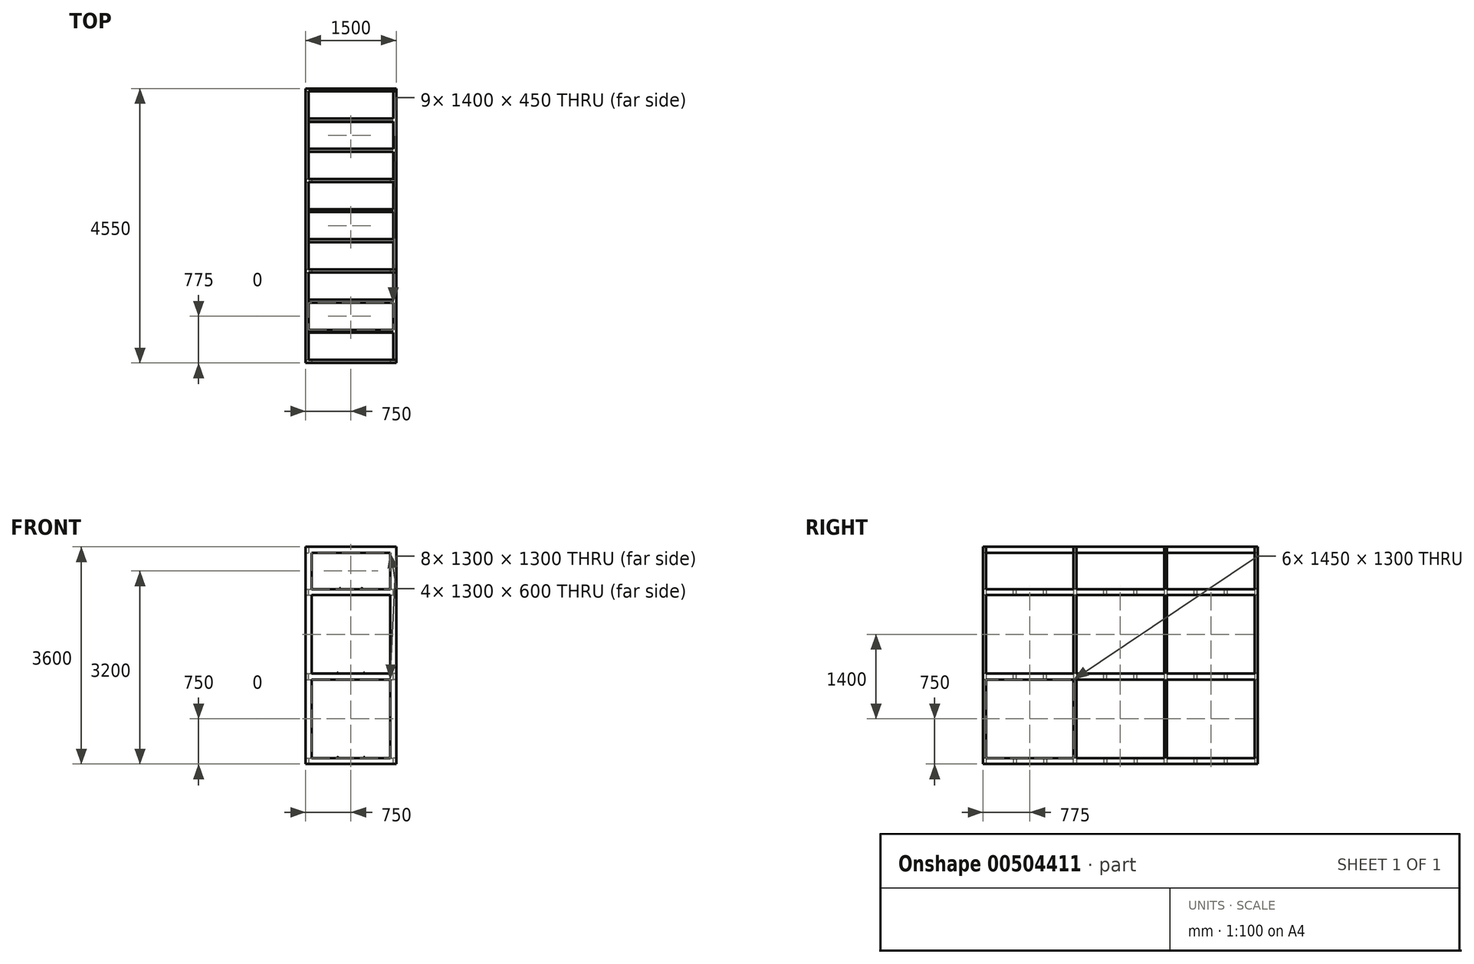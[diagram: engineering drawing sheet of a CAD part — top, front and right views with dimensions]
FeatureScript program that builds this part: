
annotation { "Feature Type Name" : "Feature", "Feature Type Description" : "" }
export const myFeature = defineFeature(function(context is Context, id is Id, definition is map)
    precondition{}
    {
        {
            var Q0;
            Q0=qCreatedBy(makeId("Front.planeOp"),FACE);
            var sketch = newSketch(context, id + "F0", { "sketchPlane" : qUnion([Q0])});
            skCircle(sketch, "E0", {"center": v(0, 700) * mm, "radius": 600 * mm});
            skCircle(sketch, "E1", {"center": v(0, 2100) * mm, "radius": 600 * mm});
            skCircle(sketch, "E2", {"center": v(0, 3275) * mm, "radius": 375 * mm});
            skSolve(sketch);
        }
        {
            var Q0;
            Q0=qCreatedBy(makeId("Front.planeOp"),FACE);
            var sketch = newSketch(context, id + "F1", { "sketchPlane" : qUnion([Q0])});
            skLineSegment(sketch, "E3.bottom", {"start": v(-750, 3600) * mm, "end": v(750, 3600) * mm});
            skLineSegment(sketch, "E3.top", {"start": v(-750, 0) * mm, "end": v(750, 0) * mm});
            skLineSegment(sketch, "E3.left", {"start": v(-750, 3600) * mm, "end": v(-750, 0) * mm});
            skLineSegment(sketch, "E3.right", {"start": v(750, 3600) * mm, "end": v(750, 0) * mm});
            skSolve(sketch);
        }
        {
            var Q0;
            Q0=makeQuery(id+"F1.imprint","IMPRINT",FACE,{"disambiguationData":[TD([[makeQuery(id+"F1.imprint","IMPRINT",EDGE,{"derivedFrom":sQuery(id+"F1.wireOp",EDGE,"E3.bottom")}),-1.0]])]});
            extrude(context, id + "F2", {"entities" : qUnion([Q0]), "depth" : 4550 * mm, "offsetDistance" : 25 * mm});
        }
        {
            var Q0;
            Q0=makeQuery(id+"F2.opExtrude","CAP_FACE",FACE,{"disambiguationData":[OSD([sQuery(id+"F1.wireOp",EDGE,"E3.bottom"),sQuery(id+"F1.wireOp",EDGE,"E3.top"),sQuery(id+"F1.wireOp",EDGE,"E3.left"),sQuery(id+"F1.wireOp",EDGE,"E3.right")])],"isStart":false});
            var sketch = newSketch(context, id + "F3", { "sketchPlane" : qUnion([Q0])});
            skLineSegment(sketch, "E4.bottom", {"start": v(-650, 1400) * mm, "end": v(650, 1400) * mm});
            skLineSegment(sketch, "E4.top", {"start": v(-650, 100) * mm, "end": v(650, 100) * mm});
            skLineSegment(sketch, "E4.left", {"start": v(-650, 1400) * mm, "end": v(-650, 100) * mm});
            skLineSegment(sketch, "E4.right", {"start": v(650, 1400) * mm, "end": v(650, 100) * mm});
            skLineSegment(sketch, "E5.bottom", {"start": v(-650, 2800) * mm, "end": v(650, 2800) * mm});
            skLineSegment(sketch, "E5.top", {"start": v(-650, 1500) * mm, "end": v(650, 1500) * mm});
            skLineSegment(sketch, "E5.left", {"start": v(-650, 2800) * mm, "end": v(-650, 1500) * mm});
            skLineSegment(sketch, "E5.right", {"start": v(650, 2800) * mm, "end": v(650, 1500) * mm});
            skLineSegment(sketch, "E6.bottom", {"start": v(-650, 3500) * mm, "end": v(650, 3500) * mm});
            skLineSegment(sketch, "E6.top", {"start": v(-650, 2900) * mm, "end": v(650, 2900) * mm});
            skLineSegment(sketch, "E6.left", {"start": v(-650, 3500) * mm, "end": v(-650, 2900) * mm});
            skLineSegment(sketch, "E6.right", {"start": v(650, 3500) * mm, "end": v(650, 2900) * mm});
            skSolve(sketch);
        }
        {
            var Q0;
            Q0=qSketchRegion(id+"F3",true);
            extrude(context, id + "F4", {"entities" : qUnion([Q0]), "operationType" : NewBodyOperationType.REMOVE, "oppositeDirection" : true, "depth" : 20000 * mm, "offsetDistance" : 25 * mm});
        }
        {
            var Q0;
            Q0=makeQuery(id+"F2.opExtrude","SWEPT_FACE",FACE,{"disambiguationData":[OSD([sQuery(id+"F1.wireOp",EDGE,"E3.right")])]});
            var sketch = newSketch(context, id + "F5", { "sketchPlane" : qUnion([Q0])});
            skLineSegment(sketch, "E7.bottom", {"start": v(-50, 4000) * mm, "end": v(-1500, 4000) * mm});
            skLineSegment(sketch, "E7.top", {"start": v(-50, 0) * mm, "end": v(-1500, 0) * mm});
            skLineSegment(sketch, "E7.left", {"start": v(-50, 4000) * mm, "end": v(-50, 0) * mm});
            skLineSegment(sketch, "E7.right", {"start": v(-1500, 4000) * mm, "end": v(-1500, 0) * mm});
            skLineSegment(sketch, "E8.bottom", {"start": v(-1550, 4014.4) * mm, "end": v(-3000, 4014.4) * mm});
            skLineSegment(sketch, "E8.top", {"start": v(-1550, -275.7) * mm, "end": v(-3000, -275.7) * mm});
            skLineSegment(sketch, "E8.left", {"start": v(-1550, 4014.4) * mm, "end": v(-1550, -275.7) * mm});
            skLineSegment(sketch, "E8.right", {"start": v(-3000, 4014.4) * mm, "end": v(-3000, -275.7) * mm});
            skLineSegment(sketch, "E9.bottom", {"start": v(-3050, 4012.1) * mm, "end": v(-4500, 4012.1) * mm});
            skLineSegment(sketch, "E9.top", {"start": v(-3050, -275.7) * mm, "end": v(-4500, -275.7) * mm});
            skLineSegment(sketch, "E9.left", {"start": v(-3050, 4012.1) * mm, "end": v(-3050, -275.7) * mm});
            skLineSegment(sketch, "E9.right", {"start": v(-4500, 4012.1) * mm, "end": v(-4500, -275.7) * mm});
            skSolve(sketch);
        }
        {
            var Q0;
            Q0=qSketchRegion(id+"F5",true);
            extrude(context, id + "F6", {"entities" : qUnion([Q0]), "operationType" : NewBodyOperationType.REMOVE, "oppositeDirection" : true, "depth" : 2000 * mm, "offsetDistance" : 25 * mm});
        }
        {
            var Q0;
            Q0=makeQuery(id+"F2.opExtrude","CAP_FACE",FACE,{"disambiguationData":[OSD([sQuery(id+"F1.wireOp",EDGE,"E3.bottom"),sQuery(id+"F1.wireOp",EDGE,"E3.top"),sQuery(id+"F1.wireOp",EDGE,"E3.left"),sQuery(id+"F1.wireOp",EDGE,"E3.right")])],"isStart":false});
            var sketch = newSketch(context, id + "F7", { "sketchPlane" : qUnion([Q0])});
            skLineSegment(sketch, "E10.bottom", {"start": v(750, 1500) * mm, "end": v(700, 1500) * mm});
            skLineSegment(sketch, "E10.top", {"start": v(750, 1400) * mm, "end": v(700, 1400) * mm});
            skLineSegment(sketch, "E10.left", {"start": v(750, 1500) * mm, "end": v(750, 1400) * mm});
            skLineSegment(sketch, "E10.right", {"start": v(700, 1500) * mm, "end": v(700, 1400) * mm});
            skLineSegment(sketch, "E11.left", {"start": v(750, 1500) * mm, "end": v(750, 1500) * mm});
            skLineSegment(sketch, "E11.right", {"start": v(700, 1500) * mm, "end": v(700, 1500) * mm});
            skLineSegment(sketch, "E12.bottom", {"start": v(-750, 3600) * mm, "end": v(-700, 3600) * mm});
            skLineSegment(sketch, "E12.top", {"start": v(-750, 3500) * mm, "end": v(-700, 3500) * mm});
            skLineSegment(sketch, "E12.left", {"start": v(-750, 3600) * mm, "end": v(-750, 3500) * mm});
            skLineSegment(sketch, "E12.right", {"start": v(-700, 3600) * mm, "end": v(-700, 3500) * mm});
            skLineSegment(sketch, "E13.bottom", {"start": v(-750, 2900) * mm, "end": v(-700, 2900) * mm});
            skLineSegment(sketch, "E13.top", {"start": v(-750, 2800) * mm, "end": v(-700, 2800) * mm});
            skLineSegment(sketch, "E13.left", {"start": v(-750, 2900) * mm, "end": v(-750, 2800) * mm});
            skLineSegment(sketch, "E13.right", {"start": v(-700, 2900) * mm, "end": v(-700, 2800) * mm});
            skLineSegment(sketch, "E14.bottom", {"start": v(-750, 1500) * mm, "end": v(-700, 1500) * mm});
            skLineSegment(sketch, "E14.top", {"start": v(-750, 1400) * mm, "end": v(-700, 1400) * mm});
            skLineSegment(sketch, "E14.left", {"start": v(-750, 1500) * mm, "end": v(-750, 1400) * mm});
            skLineSegment(sketch, "E14.right", {"start": v(-700, 1500) * mm, "end": v(-700, 1400) * mm});
            skLineSegment(sketch, "E15.bottom", {"start": v(-750, 0) * mm, "end": v(-700, 0) * mm});
            skLineSegment(sketch, "E15.top", {"start": v(-750, 100) * mm, "end": v(-700, 100) * mm});
            skLineSegment(sketch, "E15.left", {"start": v(-750, 0) * mm, "end": v(-750, 100) * mm});
            skLineSegment(sketch, "E15.right", {"start": v(-700, 0) * mm, "end": v(-700, 100) * mm});
            skLineSegment(sketch, "E16.bottom", {"start": v(750, 100) * mm, "end": v(700, 100) * mm});
            skLineSegment(sketch, "E16.top", {"start": v(750, 0) * mm, "end": v(700, 0) * mm});
            skLineSegment(sketch, "E16.left", {"start": v(750, 100) * mm, "end": v(750, 0) * mm});
            skLineSegment(sketch, "E16.right", {"start": v(700, 100) * mm, "end": v(700, 0) * mm});
            skLineSegment(sketch, "E17.bottom", {"start": v(700, 2900) * mm, "end": v(750, 2900) * mm});
            skLineSegment(sketch, "E17.top", {"start": v(700, 2800) * mm, "end": v(750, 2800) * mm});
            skLineSegment(sketch, "E17.left", {"start": v(700, 2900) * mm, "end": v(700, 2800) * mm});
            skLineSegment(sketch, "E17.right", {"start": v(750, 2900) * mm, "end": v(750, 2800) * mm});
            skSolve(sketch);
        }
        {
            var Q0;
            Q0=qSketchRegion(id+"F7",true);
            extrude(context, id + "F8", {"entities" : qUnion([Q0]), "operationType" : NewBodyOperationType.ADD, "oppositeDirection" : true, "depth" : 4550 * mm, "offsetDistance" : 25 * mm});
        }
        {
            var Q0;
            Q0=makeQuery(id+"F2.opExtrude","CAP_FACE",FACE,{"disambiguationData":[OSD([sQuery(id+"F1.wireOp",EDGE,"E3.bottom"),sQuery(id+"F1.wireOp",EDGE,"E3.top"),sQuery(id+"F1.wireOp",EDGE,"E3.left"),sQuery(id+"F1.wireOp",EDGE,"E3.right")])],"isStart":true});
            var sketch = newSketch(context, id + "F9", { "sketchPlane" : qUnion([Q0])});
            skCircle(sketch, "E18", {"center": v(-180, 2907.5) * mm, "radius": 7.5 * mm});
            skCircle(sketch, "E19", {"center": v(220, 1507.5) * mm, "radius": 7.5 * mm});
            skCircle(sketch, "E20", {"center": v(-220, 1507.5) * mm, "radius": 7.5 * mm});
            skCircle(sketch, "E21", {"center": v(220, 107.5) * mm, "radius": 7.5 * mm});
            skCircle(sketch, "E22", {"center": v(-220, 107.5) * mm, "radius": 7.5 * mm});
            skCircle(sketch, "E23", {"center": v(180, 2907.5) * mm, "radius": 7.5 * mm});
            skSolve(sketch);
        }
        {
            var Q0;
            {var subQ1=sQuery(id+"F1.wireOp",EDGE,"E3.right");Q0=makeQuery(id+"F8.boolean.opBoolean","MERGE",FACE,{"derivedFrom":[makeQuery(id+"F6.boolean.opBoolean","SPLIT",FACE,{"disambiguationData":[TD([makeQuery(id+"F6.opExtrude","SWEPT_FACE",FACE,{"disambiguationData":[OSD([sQuery(id+"F5.wireOp",EDGE,"E9.right")])]})])],"derivedFrom":makeQuery(id+"F2.opExtrude","SWEPT_FACE",FACE,{"disambiguationData":[OSD([subQ1])]})}),makeQuery(id+"F8.opExtrude","SWEPT_FACE",FACE,{"disambiguationData":[OSD([sQuery(id+"F7.wireOp",EDGE,"E10.left")])]}),makeQuery(id+"F8.opExtrude","SWEPT_FACE",FACE,{"disambiguationData":[OSD([sQuery(id+"F7.wireOp",EDGE,"E16.left")])]}),makeQuery(id+"F8.opExtrude","SWEPT_FACE",FACE,{"disambiguationData":[OSD([sQuery(id+"F7.wireOp",EDGE,"E17.right")])]})]});}
            var sketch = newSketch(context, id + "F10", { "sketchPlane" : qUnion([Q0])});
            skLineSegment(sketch, "E24.bottom", {"start": v(-4050, 2900) * mm, "end": v(-4000, 2900) * mm});
            skLineSegment(sketch, "E24.top", {"start": v(-4050, 2800) * mm, "end": v(-4000, 2800) * mm});
            skLineSegment(sketch, "E24.left", {"start": v(-4050, 2900) * mm, "end": v(-4050, 2800) * mm});
            skLineSegment(sketch, "E24.right", {"start": v(-4000, 2900) * mm, "end": v(-4000, 2800) * mm});
            skLineSegment(sketch, "E25.bottom", {"start": v(-3550, 2900) * mm, "end": v(-3500, 2900) * mm});
            skLineSegment(sketch, "E25.top", {"start": v(-3550, 2800) * mm, "end": v(-3500, 2800) * mm});
            skLineSegment(sketch, "E25.left", {"start": v(-3550, 2900) * mm, "end": v(-3550, 2800) * mm});
            skLineSegment(sketch, "E25.right", {"start": v(-3500, 2900) * mm, "end": v(-3500, 2800) * mm});
            skLineSegment(sketch, "E26.bottom", {"start": v(-2550, 2900) * mm, "end": v(-2500, 2900) * mm});
            skLineSegment(sketch, "E26.top", {"start": v(-2550, 2800) * mm, "end": v(-2500, 2800) * mm});
            skLineSegment(sketch, "E26.left", {"start": v(-2550, 2900) * mm, "end": v(-2550, 2800) * mm});
            skLineSegment(sketch, "E26.right", {"start": v(-2500, 2900) * mm, "end": v(-2500, 2800) * mm});
            skLineSegment(sketch, "E27.bottom", {"start": v(-2050, 2900) * mm, "end": v(-2000, 2900) * mm});
            skLineSegment(sketch, "E27.top", {"start": v(-2050, 2800) * mm, "end": v(-2000, 2800) * mm});
            skLineSegment(sketch, "E27.left", {"start": v(-2050, 2900) * mm, "end": v(-2050, 2800) * mm});
            skLineSegment(sketch, "E27.right", {"start": v(-2000, 2900) * mm, "end": v(-2000, 2800) * mm});
            skLineSegment(sketch, "E28.bottom", {"start": v(-1050, 2900) * mm, "end": v(-1000, 2900) * mm});
            skLineSegment(sketch, "E28.top", {"start": v(-1050, 2800) * mm, "end": v(-1000, 2800) * mm});
            skLineSegment(sketch, "E28.left", {"start": v(-1050, 2900) * mm, "end": v(-1050, 2800) * mm});
            skLineSegment(sketch, "E28.right", {"start": v(-1000, 2900) * mm, "end": v(-1000, 2800) * mm});
            skLineSegment(sketch, "E29.bottom", {"start": v(-550, 2900) * mm, "end": v(-500, 2900) * mm});
            skLineSegment(sketch, "E29.top", {"start": v(-550, 2800) * mm, "end": v(-500, 2800) * mm});
            skLineSegment(sketch, "E29.left", {"start": v(-550, 2900) * mm, "end": v(-550, 2800) * mm});
            skLineSegment(sketch, "E29.right", {"start": v(-500, 2900) * mm, "end": v(-500, 2800) * mm});
            skLineSegment(sketch, "E30.bottom", {"start": v(-4050, 1500) * mm, "end": v(-4000, 1500) * mm});
            skLineSegment(sketch, "E30.top", {"start": v(-4050, 1400) * mm, "end": v(-4000, 1400) * mm});
            skLineSegment(sketch, "E30.left", {"start": v(-4050, 1500) * mm, "end": v(-4050, 1400) * mm});
            skLineSegment(sketch, "E30.right", {"start": v(-4000, 1500) * mm, "end": v(-4000, 1400) * mm});
            skLineSegment(sketch, "E31.bottom", {"start": v(-3550, 1500) * mm, "end": v(-3500, 1500) * mm});
            skLineSegment(sketch, "E31.top", {"start": v(-3550, 1400) * mm, "end": v(-3500, 1400) * mm});
            skLineSegment(sketch, "E31.left", {"start": v(-3550, 1500) * mm, "end": v(-3550, 1400) * mm});
            skLineSegment(sketch, "E31.right", {"start": v(-3500, 1500) * mm, "end": v(-3500, 1400) * mm});
            skLineSegment(sketch, "E32.bottom", {"start": v(-2550, 1500) * mm, "end": v(-2500, 1500) * mm});
            skLineSegment(sketch, "E32.top", {"start": v(-2550, 1400) * mm, "end": v(-2500, 1400) * mm});
            skLineSegment(sketch, "E32.left", {"start": v(-2550, 1500) * mm, "end": v(-2550, 1400) * mm});
            skLineSegment(sketch, "E32.right", {"start": v(-2500, 1500) * mm, "end": v(-2500, 1400) * mm});
            skLineSegment(sketch, "E33.bottom", {"start": v(-2050, 1500) * mm, "end": v(-2000, 1500) * mm});
            skLineSegment(sketch, "E33.top", {"start": v(-2050, 1400) * mm, "end": v(-2000, 1400) * mm});
            skLineSegment(sketch, "E33.left", {"start": v(-2050, 1500) * mm, "end": v(-2050, 1400) * mm});
            skLineSegment(sketch, "E33.right", {"start": v(-2000, 1500) * mm, "end": v(-2000, 1400) * mm});
            skLineSegment(sketch, "E34.bottom", {"start": v(-1050, 1500) * mm, "end": v(-1000, 1500) * mm});
            skLineSegment(sketch, "E34.top", {"start": v(-1050, 1400) * mm, "end": v(-1000, 1400) * mm});
            skLineSegment(sketch, "E34.left", {"start": v(-1050, 1500) * mm, "end": v(-1050, 1400) * mm});
            skLineSegment(sketch, "E34.right", {"start": v(-1000, 1500) * mm, "end": v(-1000, 1400) * mm});
            skLineSegment(sketch, "E35.bottom", {"start": v(-550, 1500) * mm, "end": v(-500, 1500) * mm});
            skLineSegment(sketch, "E35.top", {"start": v(-550, 1400) * mm, "end": v(-500, 1400) * mm});
            skLineSegment(sketch, "E35.left", {"start": v(-550, 1500) * mm, "end": v(-550, 1400) * mm});
            skLineSegment(sketch, "E35.right", {"start": v(-500, 1500) * mm, "end": v(-500, 1400) * mm});
            skLineSegment(sketch, "E36.bottom", {"start": v(-4050, 100) * mm, "end": v(-4000, 100) * mm});
            skLineSegment(sketch, "E36.top", {"start": v(-4050, 0) * mm, "end": v(-4000, 0) * mm});
            skLineSegment(sketch, "E36.left", {"start": v(-4050, 100) * mm, "end": v(-4050, 0) * mm});
            skLineSegment(sketch, "E36.right", {"start": v(-4000, 100) * mm, "end": v(-4000, 0) * mm});
            skLineSegment(sketch, "E37.bottom", {"start": v(-3550, 100) * mm, "end": v(-3500, 100) * mm});
            skLineSegment(sketch, "E37.top", {"start": v(-3550, 0) * mm, "end": v(-3500, 0) * mm});
            skLineSegment(sketch, "E37.left", {"start": v(-3550, 100) * mm, "end": v(-3550, 0) * mm});
            skLineSegment(sketch, "E37.right", {"start": v(-3500, 100) * mm, "end": v(-3500, 0) * mm});
            skLineSegment(sketch, "E38.bottom", {"start": v(-2550, 100) * mm, "end": v(-2499.8, 100) * mm});
            skLineSegment(sketch, "E38.top", {"start": v(-2550, 0) * mm, "end": v(-2499.8, 0) * mm});
            skLineSegment(sketch, "E38.left", {"start": v(-2550, 100) * mm, "end": v(-2550, 0) * mm});
            skLineSegment(sketch, "E38.right", {"start": v(-2499.8, 100) * mm, "end": v(-2499.8, 0) * mm});
            skLineSegment(sketch, "E39.bottom", {"start": v(-2049.8, 100) * mm, "end": v(-2000, 100) * mm});
            skLineSegment(sketch, "E39.top", {"start": v(-2049.8, 0) * mm, "end": v(-2000, 0) * mm});
            skLineSegment(sketch, "E39.left", {"start": v(-2049.8, 100) * mm, "end": v(-2049.8, 0) * mm});
            skLineSegment(sketch, "E39.right", {"start": v(-2000, 100) * mm, "end": v(-2000, 0) * mm});
            skLineSegment(sketch, "E40.bottom", {"start": v(-1050, 100) * mm, "end": v(-1003.18, 100) * mm});
            skLineSegment(sketch, "E40.top", {"start": v(-1050, 0) * mm, "end": v(-1003.18, 0) * mm});
            skLineSegment(sketch, "E40.left", {"start": v(-1050, 100) * mm, "end": v(-1050, 0) * mm});
            skLineSegment(sketch, "E40.right", {"start": v(-1003.18, 100) * mm, "end": v(-1003.18, 0) * mm});
            skLineSegment(sketch, "E41.bottom", {"start": v(-553.18, 100) * mm, "end": v(-500, 100) * mm});
            skLineSegment(sketch, "E41.top", {"start": v(-553.18, 0) * mm, "end": v(-500, 0) * mm});
            skLineSegment(sketch, "E41.left", {"start": v(-553.18, 100) * mm, "end": v(-553.18, 0) * mm});
            skLineSegment(sketch, "E41.right", {"start": v(-500, 100) * mm, "end": v(-500, 0) * mm});
            skSolve(sketch);
        }
        {
            var Q0;
            Q0=qSketchRegion(id+"F10",true);
            extrude(context, id + "F11", {"entities" : qUnion([Q0]), "operationType" : NewBodyOperationType.ADD, "oppositeDirection" : true, "depth" : 1500 * mm, "offsetDistance" : 25 * mm});
        }
        {
            var Q0;
            Q0=qSketchRegion(id+"F9",true);
            extrude(context, id + "F12", {"entities" : qUnion([Q0]), "operationType" : NewBodyOperationType.ADD, "oppositeDirection" : true, "depth" : 50 * mm, "offsetDistance" : 25 * mm});
        }
    });
